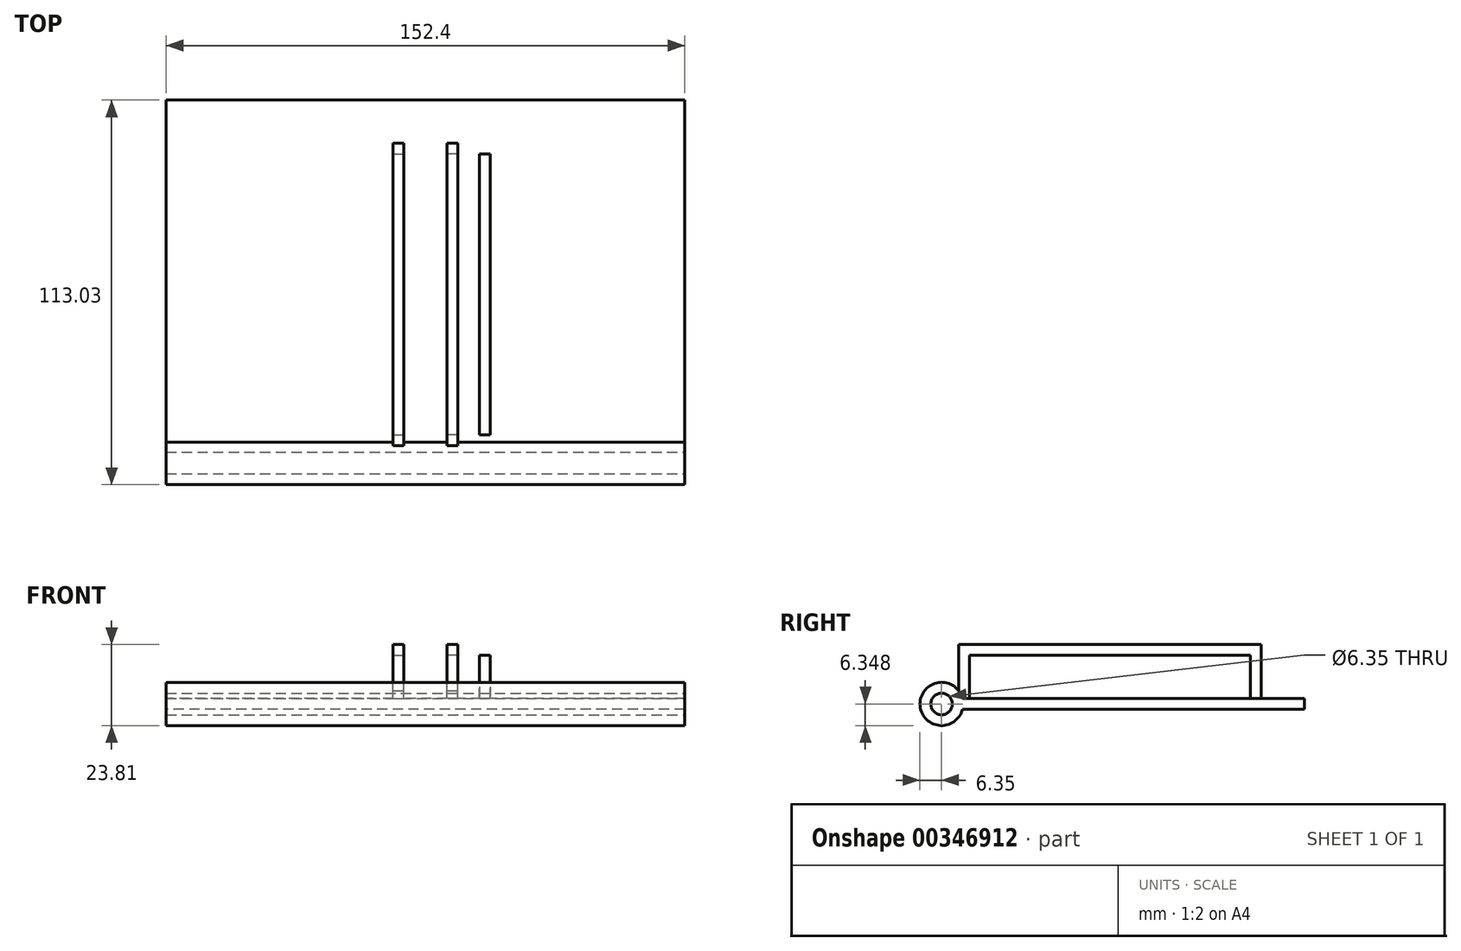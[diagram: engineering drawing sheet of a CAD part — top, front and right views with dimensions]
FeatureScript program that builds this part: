
annotation { "Feature Type Name" : "Feature", "Feature Type Description" : "" }
export const myFeature = defineFeature(function(context is Context, id is Id, definition is map)
    precondition{}
    {
        {
            var Q0;
            Q0=qCreatedBy(makeId("Top.planeOp"),FACE);
            var sketch = newSketch(context, id + "F0", { "sketchPlane" : qUnion([Q0])});
            skLineSegment(sketch, "E0.bottom", {"start": v(-76.2, 50.8) * mm, "end": v(76.2, 50.8) * mm});
            skLineSegment(sketch, "E0.top", {"start": v(-76.2, -50.8) * mm, "end": v(76.2, -50.8) * mm});
            skLineSegment(sketch, "E0.left", {"start": v(-76.2, 50.8) * mm, "end": v(-76.2, -50.8) * mm});
            skLineSegment(sketch, "E0.right", {"start": v(76.2, 50.8) * mm, "end": v(76.2, -50.8) * mm});
            skPoint(sketch, "E0.middle", {"position": v(0, 0) * mm});
            skSolve(sketch);
        }
        {
            var Q0;
            Q0=makeQuery(id+"F0.imprint","IMPRINT",FACE,{"disambiguationData":[TD([[makeQuery(id+"F0.imprint","IMPRINT",EDGE,{"derivedFrom":sQuery(id+"F0.wireOp",EDGE,"E0.bottom")}),-1.0]])]});
            extrude(context, id + "F1", {"entities" : qUnion([Q0]), "depth" : 3.17 * mm});
        }
        {
            var Q0;
            Q0=qCreatedBy(makeId("Right.planeOp"),FACE);
            var sketch = newSketch(context, id + "F2", { "sketchPlane" : qUnion([Q0])});
            skCircle(sketch, "E1", {"center": v(-55.88, 1.59) * mm, "radius": 6.35 * mm});
            skSolve(sketch);
        }
        {
            var Q0;
            Q0=makeQuery(id+"F2.imprint","IMPRINT",FACE,{"disambiguationData":[TD([[makeQuery(id+"F2.imprint","IMPRINT",EDGE,{"derivedFrom":sQuery(id+"F2.wireOp",EDGE,"E1")}),1.0]])]});
            extrude(context, id + "F3", {"entities" : qUnion([Q0]), "operationType" : NewBodyOperationType.ADD, "depth" : 76.2 * mm});
        }
        {
            var Q0;
            Q0=makeQuery(id+"F3.opExtrude","CAP_FACE",FACE,{"disambiguationData":[OSD([sQuery(id+"F2.wireOp",EDGE,"E1")])],"isStart":true});
            extrude(context, id + "F4", {"entities" : qUnion([Q0]), "operationType" : NewBodyOperationType.ADD, "depth" : 76.2 * mm});
        }
        {
            var Q0;
            Q0=makeQuery(id+"F3.boolean.opBoolean","MERGE",FACE,{"derivedFrom":[makeQuery(id+"F1.opExtrude","SWEPT_FACE",FACE,{"disambiguationData":[OSD([sQuery(id+"F0.wireOp",EDGE,"E0.right")])]}),makeQuery(id+"F3.opExtrude","CAP_FACE",FACE,{"disambiguationData":[OSD([sQuery(id+"F2.wireOp",EDGE,"E1")])],"isStart":false})]});
            var sketch = newSketch(context, id + "F5", { "sketchPlane" : qUnion([Q0])});
            skCircle(sketch, "E2", {"center": v(-55.88, 1.59) * mm, "radius": 3.17 * mm});
            skSolve(sketch);
        }
        {
            var Q0;
            Q0=makeQuery(id+"F5.imprint","IMPRINT",FACE,{"disambiguationData":[TD([[makeQuery(id+"F5.imprint","IMPRINT",EDGE,{"derivedFrom":sQuery(id+"F5.wireOp",EDGE,"E2")}),1.0]])]});
            extrude(context, id + "F6", {"entities" : qUnion([Q0]), "operationType" : NewBodyOperationType.REMOVE, "oppositeDirection" : true, "depth" : 152.4 * mm});
        }
        {
            var Q0;
            Q0=qCreatedBy(makeId("Right.planeOp"),FACE);
            var sketch = newSketch(context, id + "F7", { "sketchPlane" : qUnion([Q0])});
            skLineSegment(sketch, "E3.bottom", {"start": v(-47.63, 3.18) * mm, "end": v(47.63, 3.18) * mm});
            skLineSegment(sketch, "E3.top", {"start": v(-47.63, 15.88) * mm, "end": v(47.63, 15.88) * mm});
            skLineSegment(sketch, "E3.left", {"start": v(-47.63, 3.18) * mm, "end": v(-47.63, 15.88) * mm});
            skLineSegment(sketch, "E3.right", {"start": v(47.63, 3.18) * mm, "end": v(47.63, 15.88) * mm});
            skPoint(sketch, "E3.middle", {"position": v(0, 9.53) * mm});
            skLineSegment(sketch, "E4.bottom", {"start": v(-50.8, 3.18) * mm, "end": v(50.8, 3.18) * mm});
            skLineSegment(sketch, "E4.top", {"start": v(-50.8, 19.05) * mm, "end": v(50.8, 19.05) * mm});
            skLineSegment(sketch, "E4.left", {"start": v(-50.8, 3.18) * mm, "end": v(-50.8, 19.05) * mm});
            skLineSegment(sketch, "E4.right", {"start": v(50.8, 3.18) * mm, "end": v(50.8, 19.05) * mm});
            skSolve(sketch);
        }
        {
            var Q0;
            Q0=qCreatedBy(makeId("Right.planeOp"),FACE);
            cPlane(context, id + "F8", {"entities" : qUnion([Q0]), "cplaneType" : CPlaneType.OFFSET, "offset" : 6.35 * mm, "width" : 152.4 * mm, "height" : 152.4 * mm});
        }
        {
            var Q0;
            Q0=qCreatedBy(id+"F8.planeOp",FACE);
            var sketch = newSketch(context, id + "F9", { "sketchPlane" : qUnion([Q0])});
            skLineSegment(sketch, "E5.bottom", {"start": v(-47.62, 3.18) * mm, "end": v(34.93, 3.18) * mm});
            skLineSegment(sketch, "E5.top", {"start": v(-47.62, 15.88) * mm, "end": v(34.93, 15.88) * mm});
            skLineSegment(sketch, "E5.left", {"start": v(-47.62, 3.18) * mm, "end": v(-47.62, 15.88) * mm});
            skLineSegment(sketch, "E5.right", {"start": v(34.93, 3.18) * mm, "end": v(34.93, 15.88) * mm});
            skPoint(sketch, "E5.middle", {"position": v(-6.35, 9.53) * mm});
            skLineSegment(sketch, "E6.bottom", {"start": v(-50.8, 3.18) * mm, "end": v(38.1, 3.18) * mm});
            skLineSegment(sketch, "E6.top", {"start": v(-50.8, 19.05) * mm, "end": v(38.1, 19.05) * mm});
            skLineSegment(sketch, "E6.left", {"start": v(-50.8, 3.18) * mm, "end": v(-50.8, 19.05) * mm});
            skLineSegment(sketch, "E6.right", {"start": v(38.1, 3.18) * mm, "end": v(38.1, 19.05) * mm});
            skSolve(sketch);
        }
        {
            var Q0;
            Q0=makeQuery(id+"F9.imprint","IMPRINT",FACE,{"disambiguationData":[TD([[makeQuery(id+"F9.imprint","IMPRINT",EDGE,{"derivedFrom":sQuery(id+"F9.wireOp",EDGE,"E5.top")}),1.0]])]});
            extrude(context, id + "F10", {"entities" : qUnion([Q0]), "operationType" : NewBodyOperationType.ADD, "depth" : 3.17 * mm});
        }
        {
            var Q0;
            Q0=qCreatedBy(makeId("Right.planeOp"),FACE);
            cPlane(context, id + "F11", {"entities" : qUnion([Q0]), "cplaneType" : CPlaneType.OFFSET, "offset" : 6.35 * mm, "oppositeDirection" : true, "width" : 152.4 * mm, "height" : 152.4 * mm});
        }
        {
            var Q0;
            Q0=qCreatedBy(id+"F11.planeOp",FACE);
            var sketch = newSketch(context, id + "F12", { "sketchPlane" : qUnion([Q0])});
            skLineSegment(sketch, "E7.bottom", {"start": v(-47.62, 3.18) * mm, "end": v(34.93, 3.18) * mm});
            skLineSegment(sketch, "E7.top", {"start": v(-47.62, 15.88) * mm, "end": v(34.93, 15.88) * mm});
            skLineSegment(sketch, "E7.left", {"start": v(-47.62, 3.18) * mm, "end": v(-47.62, 15.88) * mm});
            skLineSegment(sketch, "E7.right", {"start": v(34.93, 3.18) * mm, "end": v(34.93, 15.88) * mm});
            skPoint(sketch, "E7.middle", {"position": v(-6.35, 9.52) * mm});
            skLineSegment(sketch, "E8.bottom", {"start": v(-50.8, 3.18) * mm, "end": v(38.1, 3.18) * mm});
            skLineSegment(sketch, "E8.top", {"start": v(-50.8, 19.05) * mm, "end": v(38.1, 19.05) * mm});
            skLineSegment(sketch, "E8.left", {"start": v(-50.8, 3.18) * mm, "end": v(-50.8, 19.05) * mm});
            skLineSegment(sketch, "E8.right", {"start": v(38.1, 3.18) * mm, "end": v(38.1, 19.05) * mm});
            skSolve(sketch);
        }
        {
            var Q0;
            Q0=makeQuery(id+"F12.imprint","IMPRINT",FACE,{"disambiguationData":[TD([[makeQuery(id+"F12.imprint","IMPRINT",EDGE,{"derivedFrom":sQuery(id+"F12.wireOp",EDGE,"E7.top")}),1.0]])]});
            extrude(context, id + "F13", {"entities" : qUnion([Q0]), "operationType" : NewBodyOperationType.ADD, "oppositeDirection" : true, "depth" : 3.17 * mm});
        }
        {
            var Q0;
            Q0=qCreatedBy(makeId("Right.planeOp"),FACE);
            cPlane(context, id + "F14", {"entities" : qUnion([Q0]), "cplaneType" : CPlaneType.OFFSET, "offset" : 15.88 * mm, "width" : 152.4 * mm, "height" : 152.4 * mm});
        }
        {
            var Q0;
            Q0=qCreatedBy(id+"F14.planeOp",FACE);
            var sketch = newSketch(context, id + "F15", { "sketchPlane" : qUnion([Q0])});
            skLineSegment(sketch, "E9.bottom", {"start": v(-47.62, 3.18) * mm, "end": v(34.93, 3.18) * mm});
            skPoint(sketch, "E9.middle", {"position": v(-6.35, 9.52) * mm});
            skLineSegment(sketch, "E10.bottom", {"start": v(-47.38, 3.18) * mm, "end": v(47.45, 3.18) * mm});
            skPoint(sketch, "E9.left.end.orphan", {"position": v(-47.62, 15.88) * mm});
            skPoint(sketch, "E9.right.end.orphan", {"position": v(34.93, 15.88) * mm});
            skLineSegment(sketch, "E11", {"start": v(-47.62, 3.17) * mm, "end": v(-47.62, 15.88) * mm});
            skLineSegment(sketch, "E12", {"start": v(-47.62, 15.88) * mm, "end": v(34.93, 15.88) * mm});
            skLineSegment(sketch, "E13", {"start": v(34.93, 15.88) * mm, "end": v(34.93, 3.18) * mm});
            skSolve(sketch);
        }
        {
            var Q0;
            Q0=makeQuery(id+"F15.imprint","IMPRINT",FACE,{"disambiguationData":[TD([[makeQuery(id+"F15.imprint","IMPRINT",EDGE,{"derivedFrom":sQuery(id+"F15.wireOp",EDGE,"E10.top")}),-1.0]])]});
            var Q1;
            {var subQ0=sQuery(id+"F15.wireOp",EDGE,"E11");Q1=makeQuery(id+"F15.imprint","IMPRINT",FACE,{"disambiguationData":[TD([[makeQuery(id+"F15.imprint","IMPRINT",EDGE,{"derivedFrom":subQ0}),-1.0]])]});}
            extrude(context, id + "F16", {"entities" : qUnion([Q0, Q1]), "operationType" : NewBodyOperationType.ADD, "depth" : 3.17 * mm});
        }
    });
